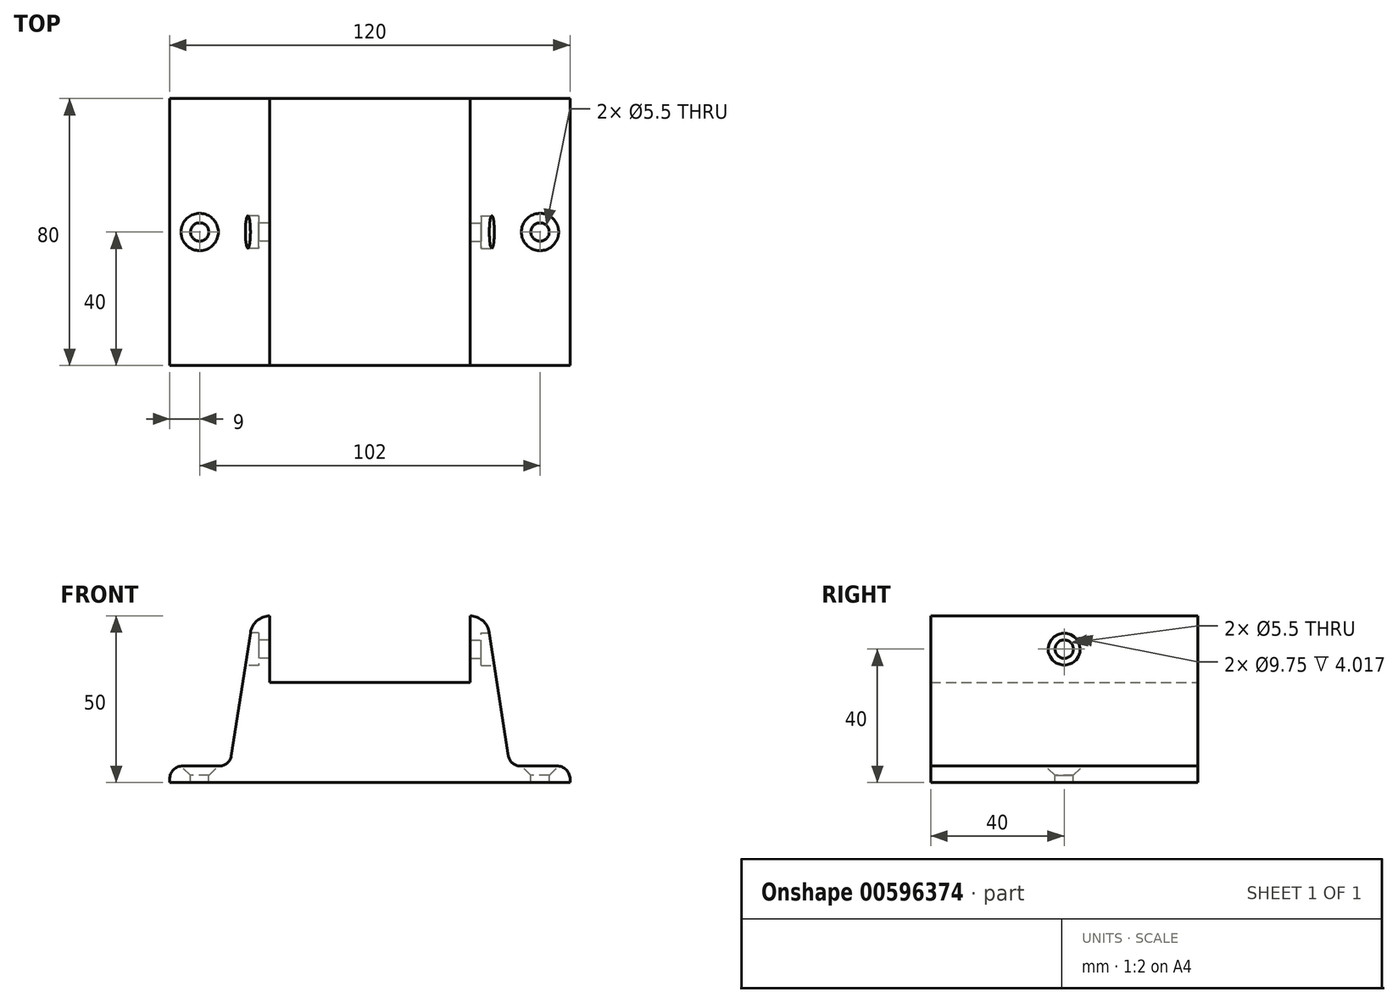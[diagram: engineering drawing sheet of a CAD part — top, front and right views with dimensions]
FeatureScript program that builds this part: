
annotation { "Feature Type Name" : "Feature", "Feature Type Description" : "" }
export const myFeature = defineFeature(function(context is Context, id is Id, definition is map)
    precondition{}
    {
        {
            var Q0;
            Q0=qCreatedBy(makeId("Front.planeOp"),FACE);
            var sketch = newSketch(context, id + "F0", { "sketchPlane" : qUnion([Q0])});
            skLineSegment(sketch, "E0", {"start": v(-60, 0) * mm, "end": v(60, 0) * mm});
            skLineSegment(sketch, "E1", {"start": v(60, 0) * mm, "end": v(60, 5) * mm});
            skLineSegment(sketch, "E2", {"start": v(60, 5) * mm, "end": v(42, 5) * mm});
            skLineSegment(sketch, "E3", {"start": v(42, 5) * mm, "end": v(35, 50) * mm});
            skLineSegment(sketch, "E4", {"start": v(35, 50) * mm, "end": v(30, 50) * mm});
            skLineSegment(sketch, "E5", {"start": v(30, 50) * mm, "end": v(30, 30) * mm});
            skLineSegment(sketch, "E6", {"start": v(30, 30) * mm, "end": v(-30, 30) * mm});
            skLineSegment(sketch, "E7", {"start": v(-30, 30) * mm, "end": v(-30, 50) * mm});
            skLineSegment(sketch, "E8", {"start": v(-30, 50) * mm, "end": v(-35, 50) * mm});
            skLineSegment(sketch, "E9", {"start": v(-35, 50) * mm, "end": v(-42, 5) * mm});
            skLineSegment(sketch, "E10", {"start": v(-42, 5) * mm, "end": v(-60, 5) * mm});
            skLineSegment(sketch, "E11", {"start": v(-60, 5) * mm, "end": v(-60, 0) * mm});
            skPoint(sketch, "E12", {"position": v(0, 30) * mm});
            skSolve(sketch);
        }
        {
            var Q0;
            Q0=makeQuery(id+"F0.imprint","IMPRINT",FACE,{"disambiguationData":[TD([[makeQuery(id+"F0.imprint","IMPRINT",EDGE,{"derivedFrom":sQuery(id+"F0.wireOp",EDGE,"E0")}),1.0]])]});
            extrude(context, id + "F1", {"entities" : qUnion([Q0]), "depth" : 80 * mm, "offsetDistance" : 25 * mm});
        }
        {
            var Q0;
            Q0=makeQuery(id+"F1.opExtrude","SWEPT_FACE",FACE,{"disambiguationData":[OSD([sQuery(id+"F0.wireOp",EDGE,"E10")])]});
            var sketch = newSketch(context, id + "F2", { "sketchPlane" : qUnion([Q0])});
            skLineSegment(sketch, "E13", {"start": v(-51, 0) * mm, "end": v(-51, -80) * mm, "construction": true});
            skPoint(sketch, "E14", {"position": v(-51, -40) * mm});
            skSolve(sketch);
        }
        {
            var Q0;
            Q0=makeQuery(id+"F1.opExtrude","SWEPT_FACE",FACE,{"disambiguationData":[OSD([sQuery(id+"F0.wireOp",EDGE,"E2")])]});
            var sketch = newSketch(context, id + "F3", { "sketchPlane" : qUnion([Q0])});
            skLineSegment(sketch, "E15", {"start": v(51, 0) * mm, "end": v(51, -80) * mm, "construction": true});
            skPoint(sketch, "E16", {"position": v(51, -40) * mm});
            skSolve(sketch);
        }
        {
            var Q0;
            Q0=makeQuery(id+"F1.opExtrude","SWEPT_FACE",FACE,{"disambiguationData":[OSD([sQuery(id+"F0.wireOp",EDGE,"E9")])]});
            var sketch = newSketch(context, id + "F4", { "sketchPlane" : qUnion([Q0])});
            skLineSegment(sketch, "E17", {"start": v(0, 21.26) * mm, "end": v(80, 21.26) * mm, "construction": true});
            skLineSegment(sketch, "E18", {"start": v(80, 21.26) * mm, "end": v(0, 21.26) * mm, "construction": true});
            skSolve(sketch);
        }
        {
            var Q0;
            Q0=makeQuery(id+"F1.opExtrude","SWEPT_FACE",FACE,{"disambiguationData":[OSD([sQuery(id+"F0.wireOp",EDGE,"E3")])]});
            var sketch = newSketch(context, id + "F5", { "sketchPlane" : qUnion([Q0])});
            skLineSegment(sketch, "E19", {"start": v(-80, 21.26) * mm, "end": v(0, 21.26) * mm, "construction": true});
            skSolve(sketch);
        }
        {
            var Q0;
            Q0=sQuery(id+"F5.wireOp",EDGE,"E19");
            cPlane(context, id + "F6", {"entities" : qUnion([Q0]), "cplaneType" : CPlaneType.LINE_ANGLE, "offset" : 25 * mm, "angle" : 90 * degree, "width" : 150 * mm, "height" : 150 * mm});
        }
        {
            var Q0;
            Q0=sQuery(id+"F4.wireOp",EDGE,"E17");
            cPlane(context, id + "F7", {"entities" : qUnion([Q0]), "cplaneType" : CPlaneType.LINE_ANGLE, "offset" : 25 * mm, "angle" : 90 * degree, "width" : 150 * mm, "height" : 150 * mm});
        }
        {
            var Q0;
            Q0=qCreatedBy(id+"F6.planeOp",FACE);
            var sketch = newSketch(context, id + "F8", { "sketchPlane" : qUnion([Q0])});
            skPoint(sketch, "E20", {"position": v(-40, 40) * mm});
            skLineSegment(sketch, "E21", {"start": v(0, 40) * mm, "end": v(-80, 40) * mm, "construction": true});
            skSolve(sketch);
        }
        {
            var Q0;
            Q0=qCreatedBy(id+"F7.planeOp",FACE);
            var sketch = newSketch(context, id + "F9", { "sketchPlane" : qUnion([Q0])});
            skPoint(sketch, "E22", {"position": v(-40, 40) * mm});
            skLineSegment(sketch, "E23", {"start": v(0, 40) * mm, "end": v(-80, 40) * mm, "construction": true});
            skSolve(sketch);
        }
        {
            var Q0;
            Q0=sQuery(id+"F2.wireOp",VERTEX,"E14");
            var Q1;
            Q1=sQuery(id+"F3.wireOp",VERTEX,"E16");
            var Q2;
            Q2=makeQuery(id+"F1.opExtrude","SWEPT_BODY",BODY,{"disambiguationData":[OSD([sQuery(id+"F0.wireOp",EDGE,"E0"),sQuery(id+"F0.wireOp",EDGE,"E1"),sQuery(id+"F0.wireOp",EDGE,"E2"),sQuery(id+"F0.wireOp",EDGE,"E3"),sQuery(id+"F0.wireOp",EDGE,"E4"),sQuery(id+"F0.wireOp",EDGE,"E5"),sQuery(id+"F0.wireOp",EDGE,"E6"),sQuery(id+"F0.wireOp",EDGE,"E7"),sQuery(id+"F0.wireOp",EDGE,"E8"),sQuery(id+"F0.wireOp",EDGE,"E9"),sQuery(id+"F0.wireOp",EDGE,"E10"),sQuery(id+"F0.wireOp",EDGE,"E11")])]});
            hole(context, id + "F10", {"style" : HoleStyle.C_SINK, "endStyle" : HoleEndStyle.BLIND, "standardTappedOrClearance" : lookupTablePath({ "standard" : "ISO", "fit" : "Normal", "size" : "M5", "type" : "Clearance" }), "standardBlindInLast" : lookupTablePath({ "fit" : "Standard", "standard" : "ISO", "size" : "M5", "type" : "Clearance" }), "holeDiameter" : 5.5 * mm, "cSinkDiameter" : 11.2 * mm, "cSinkAngle" : 90 * degree, "majorDiameter" : 5 * mm, "holeDepth" : 10 * mm, "isTappedThrough" : true, "tappedDepth" : 12 * mm, "tapClearance" : 3, "locations" : qUnion([Q0, Q1]), "scope" : qUnion([Q2])});
        }
        {
            var Q0;
            Q0=sQuery(id+"F9.wireOp",VERTEX,"E22");
            var Q1;
            Q1=makeQuery(id+"F1.opExtrude","SWEPT_BODY",BODY,{"disambiguationData":[OSD([sQuery(id+"F0.wireOp",EDGE,"E0"),sQuery(id+"F0.wireOp",EDGE,"E1"),sQuery(id+"F0.wireOp",EDGE,"E2"),sQuery(id+"F0.wireOp",EDGE,"E3"),sQuery(id+"F0.wireOp",EDGE,"E4"),sQuery(id+"F0.wireOp",EDGE,"E5"),sQuery(id+"F0.wireOp",EDGE,"E6"),sQuery(id+"F0.wireOp",EDGE,"E7"),sQuery(id+"F0.wireOp",EDGE,"E8"),sQuery(id+"F0.wireOp",EDGE,"E9"),sQuery(id+"F0.wireOp",EDGE,"E10"),sQuery(id+"F0.wireOp",EDGE,"E11")])]});
            hole(context, id + "F11", {"style" : HoleStyle.C_BORE, "endStyle" : HoleEndStyle.BLIND, "oppositeDirection" : true, "holeDiameter" : 5.5 * mm, "cBoreDiameter" : 9.75 * mm, "cBoreDepth" : 2.5 * mm, "majorDiameter" : 5 * mm, "holeDepth" : 10 * mm, "isTappedThrough" : true, "tappedDepth" : 12 * mm, "tapClearance" : 3, "locations" : qUnion([Q0]), "scope" : qUnion([Q1])});
        }
        {
            var Q0;
            Q0=sQuery(id+"F8.wireOp",VERTEX,"E20");
            var Q1;
            Q1=makeQuery(id+"F1.opExtrude","SWEPT_BODY",BODY,{"disambiguationData":[OSD([sQuery(id+"F0.wireOp",EDGE,"E0"),sQuery(id+"F0.wireOp",EDGE,"E1"),sQuery(id+"F0.wireOp",EDGE,"E2"),sQuery(id+"F0.wireOp",EDGE,"E3"),sQuery(id+"F0.wireOp",EDGE,"E4"),sQuery(id+"F0.wireOp",EDGE,"E5"),sQuery(id+"F0.wireOp",EDGE,"E6"),sQuery(id+"F0.wireOp",EDGE,"E7"),sQuery(id+"F0.wireOp",EDGE,"E8"),sQuery(id+"F0.wireOp",EDGE,"E9"),sQuery(id+"F0.wireOp",EDGE,"E10"),sQuery(id+"F0.wireOp",EDGE,"E11")])]});
            hole(context, id + "F12", {"style" : HoleStyle.C_BORE, "endStyle" : HoleEndStyle.BLIND, "holeDiameter" : 5.5 * mm, "cBoreDiameter" : 9.75 * mm, "cBoreDepth" : 2.5 * mm, "majorDiameter" : 5 * mm, "holeDepth" : 10 * mm, "isTappedThrough" : true, "tappedDepth" : 12 * mm, "tapClearance" : 3, "locations" : qUnion([Q0]), "scope" : qUnion([Q1])});
        }
        {
            var Q0;
            Q0=makeQuery(id+"F1.opExtrude","SWEPT_EDGE",EDGE,{"disambiguationData":[OSD([sQuery(id+"F0.wireOp",EDGE,"E8"),sQuery(id+"F0.wireOp",EDGE,"E9")])]});
            var Q1;
            Q1=makeQuery(id+"F1.opExtrude","SWEPT_EDGE",EDGE,{"disambiguationData":[OSD([sQuery(id+"F0.wireOp",EDGE,"E3"),sQuery(id+"F0.wireOp",EDGE,"E4")])]});
            fillet(context, id + "F13", {"entities" : qUnion([Q0, Q1]), "radius" : 6 * mm, "tangentPropagation" : true, "allowEdgeOverflow" : false});
        }
        {
            var Q0;
            Q0=makeQuery(id+"F1.opExtrude","SWEPT_EDGE",EDGE,{"disambiguationData":[OSD([sQuery(id+"F0.wireOp",EDGE,"E9"),sQuery(id+"F0.wireOp",EDGE,"E10")])]});
            var Q1;
            Q1=makeQuery(id+"F1.opExtrude","SWEPT_EDGE",EDGE,{"disambiguationData":[OSD([sQuery(id+"F0.wireOp",EDGE,"E2"),sQuery(id+"F0.wireOp",EDGE,"E3")])]});
            fillet(context, id + "F14", {"entities" : qUnion([Q0, Q1]), "radius" : 3.5 * mm, "tangentPropagation" : true, "allowEdgeOverflow" : false});
        }
        {
            var Q0;
            Q0=makeQuery(id+"F1.opExtrude","SWEPT_EDGE",EDGE,{"disambiguationData":[OSD([sQuery(id+"F0.wireOp",EDGE,"E10"),sQuery(id+"F0.wireOp",EDGE,"E11")])]});
            var Q1;
            Q1=makeQuery(id+"F1.opExtrude","SWEPT_EDGE",EDGE,{"disambiguationData":[OSD([sQuery(id+"F0.wireOp",EDGE,"E1"),sQuery(id+"F0.wireOp",EDGE,"E2")])]});
            fillet(context, id + "F15", {"entities" : qUnion([Q0, Q1]), "radius" : 4 * mm, "allowEdgeOverflow" : false});
        }
    });
